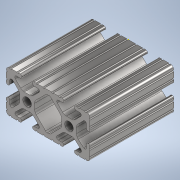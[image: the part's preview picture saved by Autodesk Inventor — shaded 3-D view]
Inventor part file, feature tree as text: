
AUTODESK INVENTOR PART (.ipt)
format: ipt  version: 2020 (Build 240168000, 168)  size: 346,112 bytes
history: native  units: in
note: dims shown in document units (in); Inventor stores cm internally (conversion verified against a paired STEP export)
features: sketch x2, extrude x1
ambient origin geometry x8: Origin, YZ Plane, XZ Plane, XY Plane, X Axis, Y Axis, Z Axis, Center Point
bodies: Solid1 (feature_tree)
feature tree (3):
  extrude  "Extrusion1"  [1 undecoded]
  sketch  "Sketch2"
  sketch  "Sketch1"  dims[d0=2.0in d1=0.0in]
note: 1 required parameter value undecoded (feature->parameter linkage not recoverable at this tier; creation-order binding heuristic only, values carry confidence <= 0.55)
